# Revit family: NBS_PressalitCareplc_Stng_NursingBench3000
name_source: partatom
category: Specialty Equipment
revit_build: Autodesk Revit 2015 (Build: 20140606_1530(x64)
units: mm (PartAtom-declared; Revit-internal decimal feet)

## types (1)
- NBS_PressalitCareplc_Stng_NursingBench3000
    Adjustable = No
    AdjustmentHeight = n/a
n/a
    AssetType = Fixed
    BIMObjectName = NBS_PressalitCareplc_Seating_NursingBench3000_R8503
    Category = Pr_40_20_06_83:Shower seats
    Depth = 967 mm  [stored 3.17257 ft]
    Description = Fixed nursing bench
    DurationUnit = year
    ElectricalDeviceNominalPower = 0
    Features = A water collection tray with integrated water outlet prevents water from splashing on carers or the floor, adjustable neck support, integrated gas cylinders enable the bench to be folded out of the way when not in use, includes brick wall fixing kit and safety rail
    Finish = Powder laquered steel, Polyurethane mattress
    Fixed = Yes
    Form = Wall mounted
    HasProtectiveEarth = Yes
    Height = 1170 mm
    HighestSeatingHeight = 0 mm  [stored 0 ft]
    IfcExportAs = IfcFurnitureType
    IfcExportType = CHAIR
    InsulationStandardClass = Unset
    IntegralAccessories = Safety Rail
    Length = 1410 mm  [stored 4.62598 ft]
    LowestSeatingHeight = 0 mm  [stored 0 ft]
    MainColor = Lead grey
    Manufacturer = www.pressalitcare.com
    ManufacturerName = Pressalit Care plc
    ManufacturerURL = www.pressalitcare.com
    MaterialsFrame = Aluminium and powder-lacquered steel
    MaterialsSeat = Polyurethane foam and plastic
    MaximumLoad = 200 kg
    ModelNumber = R8503
    ModelReference = Nursing Bench 3000, Fixed Height - R8503
    NBSCertification = www.nationalbimlibrary.com/cert/nx1qp41t
    NBSDescription = Seating
    NBSReference = 45-35-72/352
    Name = Seating_NursingBench3000_R8503_PressalitCareplc
    NominalCurrent = 0
    NominalDepth = 967 mm  [stored 3.17257 ft]
    NominalFrequencyRange = 0
    NominalHeight = 1170 mm
    NominalLength = 1410 mm  [stored 4.62598 ft]
    NominalVoltage = 0
    NominalWidth = 0 mm  [stored 0 ft]
    NumberOfPoles = 0
    NursingBenchMaterial = NBS_Concept
    PhaseAngle = 0.00°
    ProductInformation = en.pressalit.com/Handlers/Pressalit/Datasheet.ashx?area=care&id=21824&lang=en
    RailLength = 1200 mm
    SeatingHeight = 0 mm  [stored 0 ft]
    Size = 967 x 1410 mm
    Style = Bench
    Uniclass2015Description = Shower seats
    Uniclass2015Reference = Pr_40_20_06_83
    Uniclass2015Version = Products v1.3
    UsageCurrent = 0
    Version = 1
    WarrantyDescription = 3 yrs
    WarrantyDurationParts = 3
    WarrantyDurationUnit = year
    Weight = 54.2 kg
    WithSafetyRail = No

note: [stored X ft] marks values corroborated as IEEE doubles in the binary element streams (Revit-internal decimal feet)

## geometry (parser evidence)
native form markers: Sweep x11
no freeform markers — native parametric forms only
